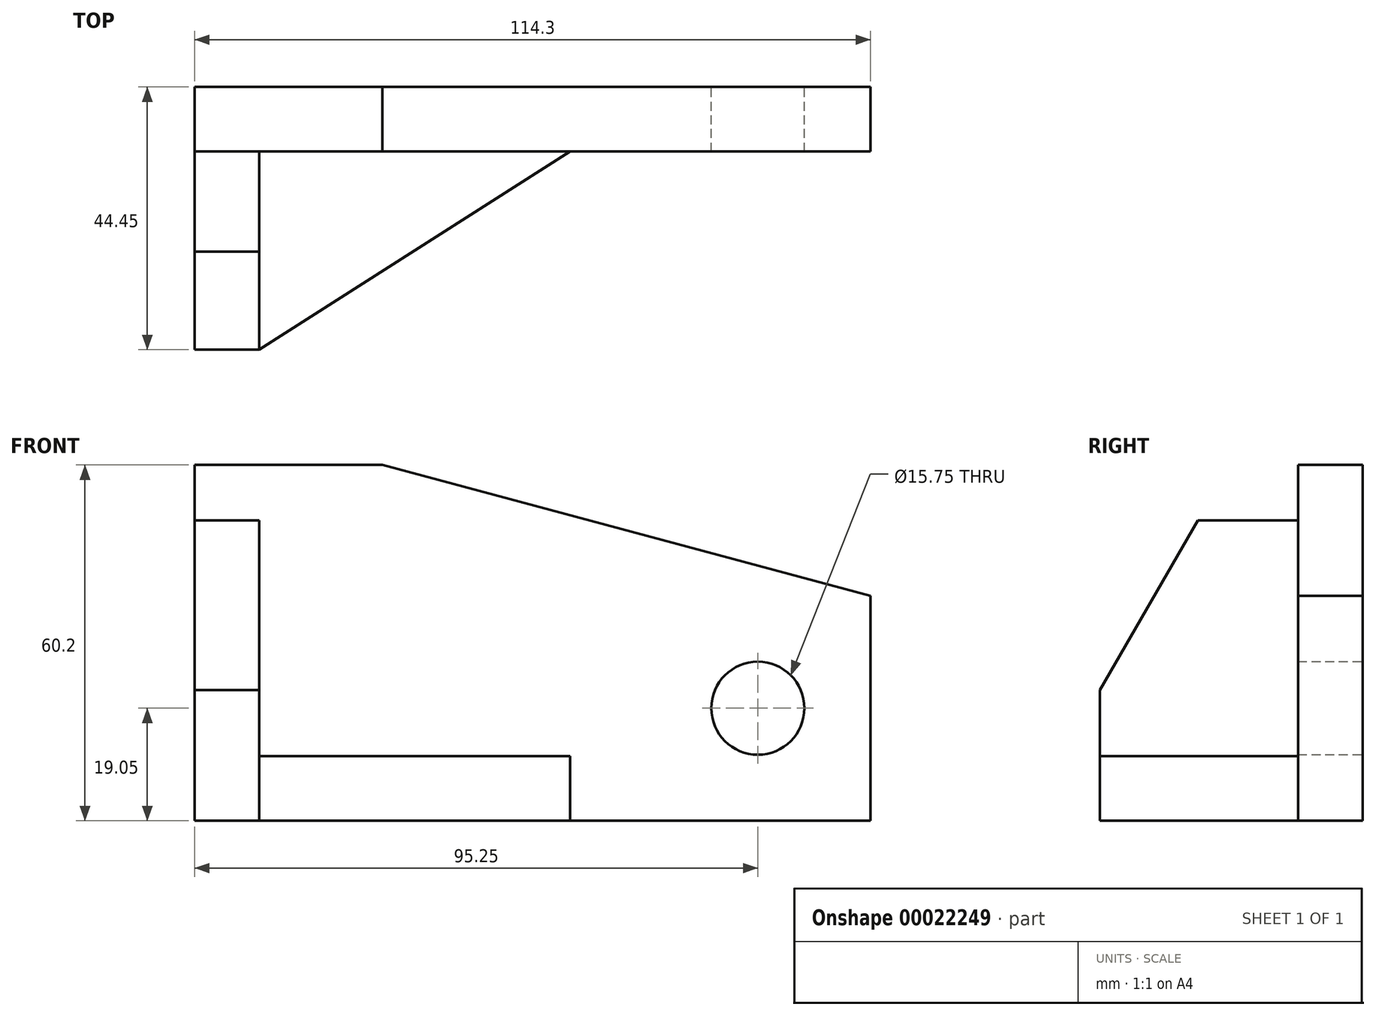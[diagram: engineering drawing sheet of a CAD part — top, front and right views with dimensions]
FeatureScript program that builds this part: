
annotation { "Feature Type Name" : "Feature", "Feature Type Description" : "" }
export const myFeature = defineFeature(function(context is Context, id is Id, definition is map)
    precondition{}
    {
        {
            var Q0;
            Q0=qCreatedBy(makeId("Front.planeOp"),FACE);
            var sketch = newSketch(context, id + "F0", { "sketchPlane" : qUnion([Q0])});
            skLineSegment(sketch, "E0.bottom", {"start": v(0, 0) * mm, "end": v(-114.3, 0) * mm});
            skLineSegment(sketch, "E0.top", {"start": v(0, 60.2) * mm, "end": v(-114.3, 60.2) * mm});
            skLineSegment(sketch, "E0.left", {"start": v(0, 0) * mm, "end": v(0, 60.2) * mm});
            skLineSegment(sketch, "E0.right", {"start": v(-114.3, 0) * mm, "end": v(-114.3, 60.2) * mm});
            skLineSegment(sketch, "E1", {"start": v(-82.55, 60.2) * mm, "end": v(0, 38.08) * mm});
            skCircle(sketch, "E2", {"center": v(-19.05, 19.05) * mm, "radius": 7.87 * mm});
            skSolve(sketch);
        }
        {
            var Q0;
            {var subQ3=sQuery(id+"F0.wireOp",EDGE,"E0.bottom");Q0=makeQuery(id+"F0.imprint","IMPRINT",FACE,{"disambiguationData":[TD([[makeQuery(id+"F0.imprint","IMPRINT",EDGE,{"derivedFrom":subQ3}),-1.0]])]});}
            extrude(context, id + "F1", {"entities" : qUnion([Q0]), "depth" : 10.92 * mm});
        }
        {
            var Q0;
            Q0=makeQuery(id+"F1.opExtrude","SWEPT_FACE",FACE,{"disambiguationData":[OSD([sQuery(id+"F0.wireOp",EDGE,"E0.right")])]});
            var sketch = newSketch(context, id + "F2", { "sketchPlane" : qUnion([Q0])});
            skLineSegment(sketch, "E3.bottom", {"start": v(10.92, 0) * mm, "end": v(44.45, 0) * mm});
            skLineSegment(sketch, "E3.top", {"start": v(10.92, 50.8) * mm, "end": v(44.45, 50.8) * mm});
            skLineSegment(sketch, "E3.left", {"start": v(10.92, 0) * mm, "end": v(10.92, 50.8) * mm});
            skLineSegment(sketch, "E3.right", {"start": v(44.45, 0) * mm, "end": v(44.45, 50.8) * mm});
            skLineSegment(sketch, "E4", {"start": v(27.88, 50.8) * mm, "end": v(44.45, 22.1) * mm});
            skSolve(sketch);
        }
        {
            var Q0;
            {var subQ2=sQuery(id+"F2.wireOp",EDGE,"E3.bottom");Q0=makeQuery(id+"F2.imprint","IMPRINT",FACE,{"disambiguationData":[TD([[makeQuery(id+"F2.imprint","IMPRINT",EDGE,{"derivedFrom":subQ2}),1.0]])]});}
            extrude(context, id + "F3", {"entities" : qUnion([Q0]), "operationType" : NewBodyOperationType.ADD, "oppositeDirection" : true, "depth" : 10.92 * mm});
        }
        {
            var Q0;
            Q0=makeQuery(id+"F3.boolean.opBoolean","MERGE",FACE,{"derivedFrom":[makeQuery(id+"F1.opExtrude","SWEPT_FACE",FACE,{"disambiguationData":[OSD([sQuery(id+"F0.wireOp",EDGE,"E0.bottom")])]}),makeQuery(id+"F3.opExtrude","SWEPT_FACE",FACE,{"disambiguationData":[OSD([sQuery(id+"F2.wireOp",EDGE,"E3.bottom")])]})]});
            var sketch = newSketch(context, id + "F4", { "sketchPlane" : qUnion([Q0])});
            skLineSegment(sketch, "E5", {"start": v(-103.38, 44.45) * mm, "end": v(-50.8, 10.92) * mm});
            skSolve(sketch);
        }
        {
            var Q0;
            Q0 = qSketchRegion(id + "F4", true);
            var Q1;
            {var subQ1=sQuery(id+"F4.wireOp",EDGE,"E5");Q1=makeQuery(id+"F4.imprint","IMPRINT",FACE,{"disambiguationData":[TD([[makeQuery(id+"F4.imprint","IMPRINT",EDGE,{"derivedFrom":subQ1}),-1.0]])]});}
            extrude(context, id + "F5", {"entities" : qUnion([Q0, Q1]), "operationType" : NewBodyOperationType.ADD, "oppositeDirection" : true, "depth" : 10.92 * mm});
        }
    });
